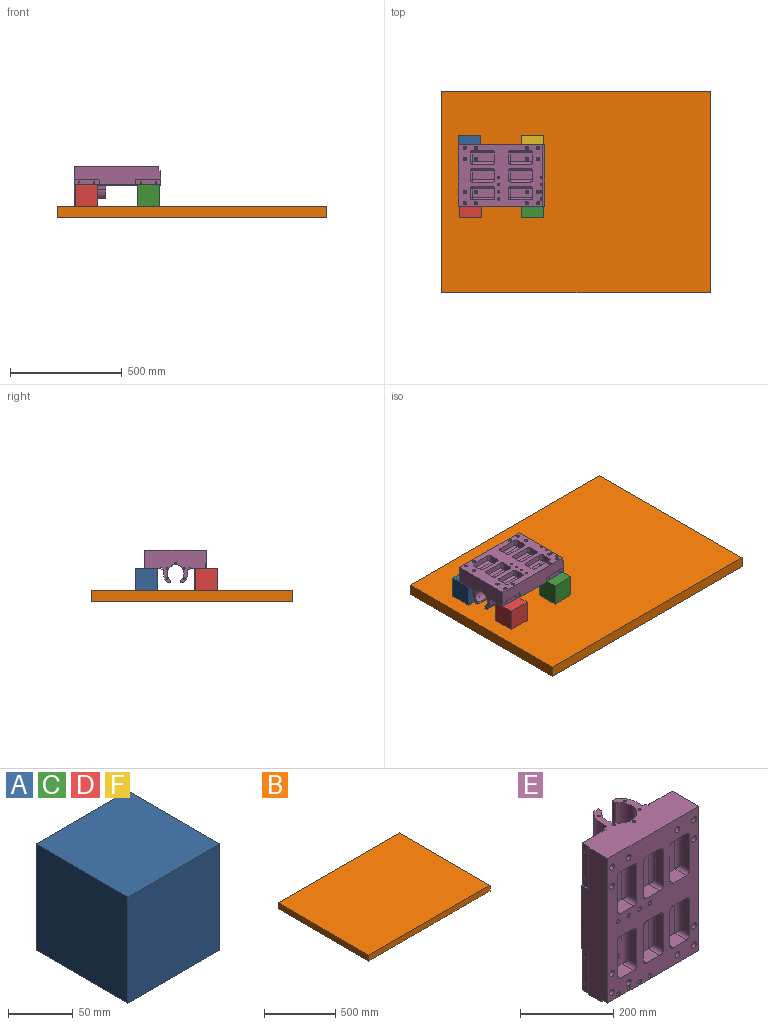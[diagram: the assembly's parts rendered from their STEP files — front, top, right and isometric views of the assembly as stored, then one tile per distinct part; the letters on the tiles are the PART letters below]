
ASSEMBLY  parts=6 mates=5
PART A: 6 faces, bbox 100x100x100 mm
  f0: plane 100x100mm, normal (0,0,1), area 10000mm2, adj f1,f3,f4,f5
  f1: plane 100x100mm, normal (-1,0,0), area 10000mm2, adj f0,f2,f4,f5
  f2: plane 100x100mm, normal (0,0,-1), area 10000mm2, adj f1,f3,f4,f5
  f3: plane 100x100mm, normal (1,0,0), area 10000mm2, adj f0,f2,f4,f5
  f4: plane 100x100mm, normal (0,-1,0), area 10000mm2, adj f0,f1,f2,f3
  f5: plane 100x100mm, normal (0,1,0), area 10000mm2, adj f0,f1,f2,f3
PART B: 6 faces, bbox 1200x900x50 mm
  f0: plane 1200x50mm, normal (0,1,0), area 60000mm2, adj f1,f3,f4,f5
  f1: plane 900x50mm, normal (-1,0,0), area 45000mm2, adj f0,f2,f4,f5
  f2: plane 1200x50mm, normal (0,-1,0), area 60000mm2, adj f1,f3,f4,f5
  f3: plane 900x50mm, normal (1,0,0), area 45000mm2, adj f0,f2,f4,f5
  f4: plane 1200x900mm, normal (0,0,1), area 1080000mm2, adj f0,f1,f2,f3
  f5: plane 1200x900mm, normal (0,0,-1), area 1080000mm2, adj f0,f1,f2,f3
PART C: same geometry as A
PART D: same geometry as A
PART E: 238 faces, bbox 275x144.8x385 mm
  f0: plane 139x14mm, normal (0,1,0), area 1946mm2, adj f2,f7,f10,f214
  f1: plane 378x275mm, normal (0,-1,0), area 62109.9mm2, adj f4,f6,f7,f42,f43,f44,f45,f47
  f2: plane 109.04x90mm, normal (0,0,-1), area 3910.3mm2, adj f0,f3,f8,f9,f10,f11,f12,f13
  f3: plane 139x17mm, normal (-1,0,0), area 2363mm2, adj f2,f7,f8,f24
  f4: plane 385x80mm, normal (-1,0,0), area 25610.7mm2, adj f1,f5,f7,f16,f18,f19,f198,f199
  f5: plane 275x66mm, normal (0,0,-1), area 14398.7mm2, adj f4,f6,f12,f13,f14,f15,f16,f17
  f6: plane 385x80mm, normal (1,0,0), area 30546.9mm2, adj f1,f5,f7,f17,f198,f199,f231,f233
  f7: plane 275x144.8mm, normal (0,0,1), area 23627.4mm2, adj f0,f1,f3,f4,f6,f8,f9,f10
  f8: cylinder r=54.52mm len=139mm, axis (0,0,1), area 6621mm2, adj f2,f3,f7,f9
  f9: plane 139x14mm, normal (0,1,0), area 1946mm2, adj f2,f7,f8,f213
  f10: cylinder r=54.52mm len=139mm, axis (0,0,1), area 6621mm2, adj f0,f2,f7,f11
  f11: plane 139x17mm, normal (1,0,0), area 2363mm2, adj f2,f7,f10,f22
  f12: plane 246x30mm, normal (0.85,0.52,0), area 8650mm2, adj f2,f5,f13,f23
  f13: plane 246x70mm, normal (0,1,0), area 17220mm2, adj f2,f5,f12,f14
  f14: plane 246x30mm, normal (-0.85,0.52,0), area 8650mm2, adj f2,f5,f13,f21
  f15: plane 385x8mm, normal (1,0,0), area 3080mm2, adj f5,f7,f22,f218
  f16: plane 385x69mm, normal (0,1,0), area 25396.1mm2, adj f4,f5,f7,f18,f20,f126,f129,f133
  f17: plane 385x71mm, normal (0,1,0), area 26826.1mm2, adj f5,f6,f7,f138,f141,f144,f147,f156
  f18: plane 18x3mm, normal (0,0,-1), area 54mm2, adj f4,f16,f20,f228
  f19: plane 105x3mm, normal (0,1,0), area 315mm2, adj f4,f5,f20,f228
  f20: plane 110x23mm, normal (-1,0,0), area 2467.1mm2, adj f5,f16,f18,f19,f28,f31,f228
  f21: plane 246x1.2mm, normal (-1,0,0), area 295.2mm2, adj f2,f5,f14,f22
  f22: plane 385x9.16mm, normal (0,1,0), area 3362.5mm2, adj f2,f5,f7,f11,f15,f21
  f23: plane 246x1.2mm, normal (1,0,0), area 295.2mm2, adj f2,f5,f12,f24
  f24: plane 385x11.16mm, normal (0,1,0), area 4132.5mm2, adj f2,f3,f5,f7,f23,f25
  f25: plane 385x8mm, normal (-1,0,0), area 3080mm2, adj f5,f7,f24,f215
  f26: cone r=2.5mm half-angle=59deg, axis (-1,0,0), area 22.9mm2, adj f27
  f27: cylinder r=2.5mm len=14.48mm, axis (-1,0,0), area 227.4mm2, adj f26,f28
  f28: cone r=3.02mm half-angle=45deg, axis (-1,0,0), area 12.9mm2, adj f20,f27
  f29: cone r=2.5mm half-angle=59deg, axis (-1,0,0), area 22.9mm2, adj f30
  f30: cylinder r=2.5mm len=14.48mm, axis (-1,0,0), area 227.4mm2, adj f29,f31
  f31: cone r=3.02mm half-angle=45deg, axis (-1,0,0), area 12.9mm2, adj f20,f30
  f32: cone r=3.4mm half-angle=59deg, axis (0,0,1), area 42.4mm2, adj f33
  f33: cylinder r=3.4mm len=23.8mm, axis (0,0,1), area 508.4mm2, adj f7,f32
  f34: cone r=3.4mm half-angle=59deg, axis (0,0,1), area 42.4mm2, adj f35
  f35: cylinder r=3.4mm len=23.8mm, axis (0,0,1), area 508.4mm2, adj f7,f34
  f36: cone r=3.4mm half-angle=59deg, axis (0,0,1), area 42.4mm2, adj f37
  f37: cylinder r=3.4mm len=23.8mm, axis (0,0,1), area 508.4mm2, adj f7,f36
  f38: cone r=3.4mm half-angle=59deg, axis (0,0,1), area 42.4mm2, adj f39
  f39: cylinder r=3.4mm len=23.8mm, axis (0,0,1), area 508.4mm2, adj f7,f38
  f40: cone r=3.4mm half-angle=59deg, axis (0,0,1), area 42.4mm2, adj f41
  f41: cylinder r=3.4mm len=23.8mm, axis (0,0,1), area 508.4mm2, adj f7,f40
  f42: plane 90x25mm, normal (1,0,0), area 2250mm2, adj f1,f90,f91,f92
  f43: plane 40x25mm, normal (0,0,-1), area 1000mm2, adj f1,f92,f94,f95
  f44: plane 90x25mm, normal (-1,0,0), area 2250mm2, adj f1,f95,f97,f98
  f45: plane 40x35mm, normal (0,0,1), area 1400mm2, adj f1,f46,f90,f98
  f46: plane 100x40mm, normal (0,-1,0), area 3823.3mm2, adj f45,f91,f94,f97,f155
  f47: plane 90x25mm, normal (1,0,0), area 2250mm2, adj f1,f72,f73,f74
  f48: plane 40x25mm, normal (0,0,-1), area 1000mm2, adj f1,f74,f78,f80
  f49: plane 90x25mm, normal (-1,0,0), area 2250mm2, adj f1,f75,f77,f80
  f50: plane 40x35mm, normal (0,0,1), area 1400mm2, adj f1,f51,f72,f75
  f51: plane 100x40mm, normal (0,-1,0), area 4000mm2, adj f50,f73,f77,f78
  f52: plane 90x25mm, normal (1,0,0), area 2250mm2, adj f1,f81,f82,f83
  f53: plane 40x25mm, normal (0,0,-1), area 1000mm2, adj f1,f83,f87,f89
  f54: plane 90x25mm, normal (-1,0,0), area 2250mm2, adj f1,f84,f86,f89
  f55: plane 40x35mm, normal (0,0,1), area 1400mm2, adj f1,f56,f81,f84
  f56: plane 100x40mm, normal (0,-1,0), area 3823.3mm2, adj f55,f82,f86,f87,f158
  f57: plane 40x35mm, normal (0,0,1), area 1400mm2, adj f1,f61,f99,f107
  f58: plane 90x25mm, normal (1,0,0), area 2250mm2, adj f1,f103,f106,f107
  f59: plane 40x25mm, normal (0,0,-1), area 1000mm2, adj f1,f100,f103,f104
  f60: plane 90x25mm, normal (-1,0,0), area 2250mm2, adj f1,f99,f100,f101
  f61: plane 100x40mm, normal (0,-1,0), area 3823.3mm2, adj f57,f101,f104,f106,f149
  f62: plane 90x25mm, normal (1,0,0), area 2250mm2, adj f1,f112,f115,f116
  f63: plane 40x25mm, normal (0,0,-1), area 1000mm2, adj f1,f109,f112,f113
  f64: plane 90x25mm, normal (-1,0,0), area 2250mm2, adj f1,f108,f109,f110
  f65: plane 40x35mm, normal (0,0,1), area 1400mm2, adj f1,f66,f108,f116
  f66: plane 100x40mm, normal (0,-1,0), area 4000mm2, adj f65,f110,f113,f115
  f67: plane 90x25mm, normal (1,0,0), area 2250mm2, adj f1,f121,f124,f125
  f68: plane 40x25mm, normal (0,0,-1), area 1000mm2, adj f1,f118,f121,f122
  f69: plane 90x25mm, normal (-1,0,0), area 2250mm2, adj f1,f117,f118,f119
  f70: plane 40x35mm, normal (0,0,1), area 1400mm2, adj f1,f71,f117,f125
  f71: plane 100x40mm, normal (0,-1,0), area 3823.3mm2, adj f70,f119,f122,f124,f132
  f72: cylinder r=10mm len=35mm, axis (0,1,0), area 492.7mm2, adj f1,f47,f50,f73
  f73: cylinder r=10mm len=100mm, axis (0,0,-1), area 1513.7mm2, adj f47,f51,f72,f76
  f74: cylinder r=10mm len=25mm, axis (0,1,0), area 392.7mm2, adj f1,f47,f48,f76
  f75: cylinder r=10mm len=35mm, axis (0,1,0), area 492.7mm2, adj f1,f49,f50,f77
  f76: sphere r=10mm, area 157.1mm2, adj f73,f74,f78
  f77: cylinder r=10mm len=100mm, axis (0,0,1), area 1513.7mm2, adj f49,f51,f75,f79
  f78: cylinder r=10mm len=40mm, axis (-1,0,0), area 628.3mm2, adj f48,f51,f76,f79
  f79: sphere r=10mm, area 157.1mm2, adj f77,f78,f80
  f80: cylinder r=10mm len=25mm, axis (0,1,0), area 392.7mm2, adj f1,f48,f49,f79
  f81: cylinder r=10mm len=35mm, axis (0,1,0), area 492.7mm2, adj f1,f52,f55,f82
  f82: cylinder r=10mm len=100mm, axis (0,0,-1), area 1513.7mm2, adj f52,f56,f81,f85
  f83: cylinder r=10mm len=25mm, axis (0,1,0), area 392.7mm2, adj f1,f52,f53,f85
  f84: cylinder r=10mm len=35mm, axis (0,1,0), area 492.7mm2, adj f1,f54,f55,f86
  f85: sphere r=10mm, area 157.1mm2, adj f82,f83,f87
  f86: cylinder r=10mm len=100mm, axis (0,0,1), area 1513.7mm2, adj f54,f56,f84,f88
  f87: cylinder r=10mm len=40mm, axis (-1,0,0), area 628.3mm2, adj f53,f56,f85,f88
  f88: sphere r=10mm, area 157.1mm2, adj f86,f87,f89
  f89: cylinder r=10mm len=25mm, axis (0,1,0), area 392.7mm2, adj f1,f53,f54,f88
  f90: cylinder r=10mm len=35mm, axis (0,1,0), area 492.7mm2, adj f1,f42,f45,f91
  f91: cylinder r=10mm len=100mm, axis (0,0,-1), area 1513.7mm2, adj f42,f46,f90,f93
  f92: cylinder r=10mm len=25mm, axis (0,1,0), area 392.7mm2, adj f1,f42,f43,f93
  f93: sphere r=10mm, area 157.1mm2, adj f91,f92,f94
  f94: cylinder r=10mm len=40mm, axis (-1,0,0), area 628.3mm2, adj f43,f46,f93,f96
  f95: cylinder r=10mm len=25mm, axis (0,1,0), area 392.7mm2, adj f1,f43,f44,f96
  f96: sphere r=10mm, area 157.1mm2, adj f94,f95,f97
  f97: cylinder r=10mm len=100mm, axis (0,0,1), area 1513.7mm2, adj f44,f46,f96,f98
  f98: cylinder r=10mm len=35mm, axis (0,1,0), area 492.7mm2, adj f1,f44,f45,f97
  f99: cylinder r=10mm len=35mm, axis (0,1,0), area 492.7mm2, adj f1,f57,f60,f101
  f100: cylinder r=10mm len=25mm, axis (0,1,0), area 392.7mm2, adj f1,f59,f60,f102
  f101: cylinder r=10mm len=100mm, axis (0,0,1), area 1513.7mm2, adj f60,f61,f99,f102
  f102: sphere r=10mm, area 157.1mm2, adj f100,f101,f104
  f103: cylinder r=10mm len=25mm, axis (0,1,0), area 392.7mm2, adj f1,f58,f59,f105
  f104: cylinder r=10mm len=40mm, axis (-1,0,0), area 628.3mm2, adj f59,f61,f102,f105
  f105: sphere r=10mm, area 157.1mm2, adj f103,f104,f106
  f106: cylinder r=10mm len=100mm, axis (0,0,-1), area 1513.7mm2, adj f58,f61,f105,f107
  f107: cylinder r=10mm len=35mm, axis (0,1,0), area 492.7mm2, adj f1,f57,f58,f106
  f108: cylinder r=10mm len=35mm, axis (0,1,0), area 492.7mm2, adj f1,f64,f65,f110
  f109: cylinder r=10mm len=25mm, axis (0,1,0), area 392.7mm2, adj f1,f63,f64,f111
  f110: cylinder r=10mm len=100mm, axis (0,0,-1), area 1513.7mm2, adj f64,f66,f108,f111
  f111: sphere r=10mm, area 157.1mm2, adj f109,f110,f113
  f112: cylinder r=10mm len=25mm, axis (0,1,0), area 392.7mm2, adj f1,f62,f63,f114
  f113: cylinder r=10mm len=40mm, axis (1,0,0), area 628.3mm2, adj f63,f66,f111,f114
  f114: sphere r=10mm, area 157.1mm2, adj f112,f113,f115
  f115: cylinder r=10mm len=100mm, axis (0,0,1), area 1513.7mm2, adj f62,f66,f114,f116
  f116: cylinder r=10mm len=35mm, axis (0,1,0), area 492.7mm2, adj f1,f62,f65,f115
  f117: cylinder r=10mm len=35mm, axis (0,1,0), area 492.7mm2, adj f1,f69,f70,f119
  f118: cylinder r=10mm len=25mm, axis (0,1,0), area 392.7mm2, adj f1,f68,f69,f120
  f119: cylinder r=10mm len=100mm, axis (0,0,-1), area 1513.7mm2, adj f69,f71,f117,f120
  f120: sphere r=10mm, area 157.1mm2, adj f118,f119,f122
  f121: cylinder r=10mm len=25mm, axis (0,1,0), area 392.7mm2, adj f1,f67,f68,f123
  f122: cylinder r=10mm len=40mm, axis (1,0,0), area 628.3mm2, adj f68,f71,f120,f123
  f123: sphere r=10mm, area 157.1mm2, adj f121,f122,f124
  f124: cylinder r=10mm len=100mm, axis (0,0,1), area 1513.7mm2, adj f67,f71,f123,f125
  f125: cylinder r=10mm len=35mm, axis (0,1,0), area 492.7mm2, adj f1,f67,f70,f124
  f126: cylinder r=4.5mm len=30mm, axis (0,-1,0), area 848.2mm2, adj f16,f127
  f127: plane 15x15mm, normal (0,-1,0), area 113.1mm2, adj f126,f128
  f128: cylinder r=7.5mm len=50mm, axis (0,-1,0), area 2356.2mm2, adj f1,f127
  f129: cylinder r=4.5mm len=30mm, axis (0,-1,0), area 848.2mm2, adj f16,f130
  f130: plane 15x15mm, normal (0,-1,0), area 113.1mm2, adj f129,f131
  f131: cylinder r=7.5mm len=50mm, axis (0,-1,0), area 2356.2mm2, adj f1,f130
  f132: cylinder r=7.5mm len=15mm, axis (0,-1,0), area 706.9mm2, adj f71,f134
  f133: cylinder r=4.5mm len=30mm, axis (0,-1,0), area 848.2mm2, adj f16,f134
  f134: plane 15x15mm, normal (0,-1,0), area 113.1mm2, adj f132,f133
  f135: cylinder r=4.5mm len=30mm, axis (0,-1,0), area 848.2mm2, adj f16,f136
  f136: plane 15x15mm, normal (0,-1,0), area 113.1mm2, adj f135,f137
  f137: cylinder r=7.5mm len=50mm, axis (0,-1,0), area 2356.2mm2, adj f1,f136
  f138: cylinder r=4.5mm len=30mm, axis (0,-1,0), area 848.2mm2, adj f17,f139
  f139: plane 15x15mm, normal (0,-1,0), area 113.1mm2, adj f138,f140
  f140: cylinder r=7.5mm len=50mm, axis (0,-1,0), area 2356.2mm2, adj f1,f139
  f141: cylinder r=4.5mm len=30mm, axis (0,-1,0), area 848.2mm2, adj f17,f142
  f142: plane 15x15mm, normal (0,-1,0), area 113.1mm2, adj f141,f143
  f143: cylinder r=7.5mm len=50mm, axis (0,-1,0), area 2356.2mm2, adj f1,f142
  f144: cylinder r=4.5mm len=30mm, axis (0,-1,0), area 848.2mm2, adj f17,f145
  f145: plane 15x15mm, normal (0,-1,0), area 113.1mm2, adj f144,f146
  f146: cylinder r=7.5mm len=50mm, axis (0,-1,0), area 2356.2mm2, adj f1,f145
  f147: cylinder r=4.5mm len=30mm, axis (0,-1,0), area 848.2mm2, adj f17,f148
  f148: plane 15x15mm, normal (0,-1,0), area 113.1mm2, adj f147,f149
  f149: cylinder r=7.5mm len=15mm, axis (0,-1,0), area 706.9mm2, adj f61,f148
  f150: cylinder r=4.5mm len=30mm, axis (0,-1,0), area 848.2mm2, adj f16,f151
  f151: plane 15x15mm, normal (0,-1,0), area 113.1mm2, adj f150,f152
  f152: cylinder r=7.5mm len=50mm, axis (0,-1,0), area 2356.2mm2, adj f1,f151
  f153: cylinder r=4.5mm len=30mm, axis (0,-1,0), area 848.2mm2, adj f16,f154
  f154: plane 15x15mm, normal (0,-1,0), area 113.1mm2, adj f153,f155
  f155: cylinder r=7.5mm len=15mm, axis (0,-1,0), area 706.9mm2, adj f46,f154
  f156: cylinder r=4.5mm len=30mm, axis (0,-1,0), area 848.2mm2, adj f17,f157
  f157: plane 15x15mm, normal (0,-1,0), area 113.1mm2, adj f156,f158
  f158: cylinder r=7.5mm len=15mm, axis (0,-1,0), area 706.9mm2, adj f56,f157
  f159: cylinder r=4.5mm len=30mm, axis (0,-1,0), area 848.2mm2, adj f17,f160
  f160: plane 15x15mm, normal (0,-1,0), area 113.1mm2, adj f159,f161
  f161: cylinder r=7.5mm len=50mm, axis (0,-1,0), area 2356.2mm2, adj f1,f160
  f162: cylinder r=4.5mm len=30mm, axis (0,-1,0), area 848.2mm2, adj f17,f163
  f163: plane 15x15mm, normal (0,-1,0), area 113.1mm2, adj f162,f164
  f164: cylinder r=7.5mm len=50mm, axis (0,-1,0), area 2356.2mm2, adj f1,f163
  f165: cylinder r=4.5mm len=30mm, axis (0,-1,0), area 848.2mm2, adj f17,f166
  f166: plane 15x15mm, normal (0,-1,0), area 113.1mm2, adj f165,f167
  f167: cylinder r=7.5mm len=50mm, axis (0,-1,0), area 2356.2mm2, adj f1,f166
  f168: cylinder r=4.5mm len=30mm, axis (0,-1,0), area 848.2mm2, adj f16,f169
  f169: plane 15x15mm, normal (0,-1,0), area 113.1mm2, adj f168,f170
  f170: cylinder r=7.5mm len=50mm, axis (0,-1,0), area 2356.2mm2, adj f1,f169
  f171: cylinder r=4.5mm len=30mm, axis (0,-1,0), area 848.2mm2, adj f16,f172
  f172: plane 15x15mm, normal (0,-1,0), area 113.1mm2, adj f171,f173
  f173: cylinder r=7.5mm len=50mm, axis (0,-1,0), area 2356.2mm2, adj f1,f172
  f174: cone r=4.4mm half-angle=59deg, axis (0,-1,0), area 71mm2, adj f175
  f175: cylinder r=4.4mm len=23.18mm, axis (0,-1,0), area 640.7mm2, adj f174,f176
  f176: cone r=5.03mm half-angle=45deg, axis (0,-1,0), area 26.2mm2, adj f1,f175
  f177: cone r=4.4mm half-angle=59deg, axis (0,-1,0), area 71mm2, adj f178
  f178: cylinder r=4.4mm len=23.18mm, axis (0,-1,0), area 640.7mm2, adj f177,f179
  f179: cone r=5.03mm half-angle=45deg, axis (0,-1,0), area 26.2mm2, adj f1,f178
  f180: cone r=4.4mm half-angle=59deg, axis (0,-1,0), area 71mm2, adj f181
  f181: cylinder r=4.4mm len=23.18mm, axis (0,-1,0), area 640.7mm2, adj f180,f182
  f182: cone r=5.03mm half-angle=45deg, axis (0,-1,0), area 26.2mm2, adj f1,f181
  f183: cone r=4.4mm half-angle=59deg, axis (0,-1,0), area 71mm2, adj f184
  f184: cylinder r=4.4mm len=23.18mm, axis (0,-1,0), area 640.7mm2, adj f183,f185
  f185: cone r=5.03mm half-angle=45deg, axis (0,-1,0), area 26.2mm2, adj f1,f184
  f186: cone r=4.4mm half-angle=59deg, axis (0,-1,0), area 71mm2, adj f187
  f187: cylinder r=4.4mm len=23.18mm, axis (0,-1,0), area 640.7mm2, adj f186,f188
  f188: cone r=5.03mm half-angle=45deg, axis (0,-1,0), area 26.2mm2, adj f1,f187
  f189: cone r=4.4mm half-angle=59deg, axis (0,-1,0), area 71mm2, adj f190
  f190: cylinder r=4.4mm len=23.18mm, axis (0,-1,0), area 640.7mm2, adj f189,f191
  f191: cone r=5.03mm half-angle=45deg, axis (0,-1,0), area 26.2mm2, adj f1,f190
  f192: cone r=4.4mm half-angle=59deg, axis (0,-1,0), area 71mm2, adj f193
  f193: cylinder r=4.4mm len=23.18mm, axis (0,-1,0), area 640.7mm2, adj f192,f194
  f194: cone r=5.03mm half-angle=45deg, axis (0,-1,0), area 26.2mm2, adj f1,f193
  f195: cone r=4.4mm half-angle=59deg, axis (0,-1,0), area 71mm2, adj f196
  f196: cylinder r=4.4mm len=23.18mm, axis (0,-1,0), area 640.7mm2, adj f195,f197
  f197: cone r=5.03mm half-angle=45deg, axis (0,-1,0), area 26.2mm2, adj f1,f196
  f198: plane 275x7mm, normal (0,-1,0), area 1925mm2, adj f4,f5,f6,f199
  f199: plane 275x20mm, normal (0,0,-1), area 5296.4mm2, adj f1,f4,f6,f198,f202,f205,f208,f211
  f200: cone r=3.4mm half-angle=59deg, axis (0,0,-1), area 42.4mm2, adj f201
  f201: cylinder r=3.4mm len=19.18mm, axis (0,0,-1), area 409.6mm2, adj f200,f202
  f202: cone r=4.03mm half-angle=45deg, axis (0,0,-1), area 20.6mm2, adj f199,f201
  f203: cone r=3.4mm half-angle=59deg, axis (0,0,-1), area 42.4mm2, adj f204
  f204: cylinder r=3.4mm len=19.18mm, axis (0,0,-1), area 409.6mm2, adj f203,f205
  f205: cone r=4.03mm half-angle=45deg, axis (0,0,-1), area 20.6mm2, adj f199,f204
  f206: cone r=3.4mm half-angle=59deg, axis (0,0,-1), area 42.4mm2, adj f207
  f207: cylinder r=3.4mm len=19.18mm, axis (0,0,-1), area 409.6mm2, adj f206,f208
  f208: cone r=4.03mm half-angle=45deg, axis (0,0,-1), area 20.6mm2, adj f199,f207
  f209: cone r=3.4mm half-angle=59deg, axis (0,0,-1), area 42.4mm2, adj f210
  f210: cylinder r=3.4mm len=19.18mm, axis (0,0,-1), area 409.6mm2, adj f209,f211
  f211: cone r=4.03mm half-angle=45deg, axis (0,0,-1), area 20.6mm2, adj f199,f210
  f212: cylinder r=38mm len=139mm, axis (0,0,1), area 27002.4mm2, adj f2,f7,f213,f214
  f213: plane 139x10.13mm, normal (1,0,0), area 1408mm2, adj f2,f7,f9,f212
  f214: plane 139x10.13mm, normal (-1,0,0), area 1408mm2, adj f0,f2,f7,f212
  f215: plane 385x4mm, normal (0,1,0), area 1540mm2, adj f5,f7,f25,f216
  f216: plane 385x2mm, normal (1,0,0), area 770mm2, adj f5,f7,f16,f215
  f217: plane 385x2mm, normal (-1,0,0), area 770mm2, adj f5,f7,f17,f218
  f218: plane 385x4mm, normal (0,1,0), area 1540mm2, adj f5,f7,f15,f217
  f219: plane 105x3mm, normal (0,1,0), area 315mm2, adj f4,f7,f221,f229
  f220: plane 18x3mm, normal (0,0,1), area 54mm2, adj f4,f16,f221,f229
  f221: plane 110x23mm, normal (-1,0,0), area 2467.1mm2, adj f7,f16,f219,f220,f224,f227,f229
  f222: cone r=2.5mm half-angle=59deg, axis (-1,0,0), area 22.9mm2, adj f223
  f223: cylinder r=2.5mm len=14.48mm, axis (-1,0,0), area 227.4mm2, adj f222,f224
  f224: cone r=3.02mm half-angle=45deg, axis (-1,0,0), area 12.9mm2, adj f221,f223
  f225: cone r=2.5mm half-angle=59deg, axis (-1,0,0), area 22.9mm2, adj f226
  f226: cylinder r=2.5mm len=14.48mm, axis (-1,0,0), area 227.4mm2, adj f225,f227
  f227: cone r=3.02mm half-angle=45deg, axis (-1,0,0), area 12.9mm2, adj f221,f226
  f228: cylinder r=5mm len=5mm, axis (1,0,0), area 23.6mm2, adj f4,f18,f19,f20
  f229: cylinder r=5mm len=5mm, axis (1,0,0), area 23.6mm2, adj f4,f219,f220,f221
  f230: cone r=3mm half-angle=59deg, axis (1,0,0), area 33mm2, adj f231
  f231: cylinder r=3mm len=20mm, axis (1,0,0), area 377mm2, adj f6,f230
  f232: cone r=3mm half-angle=59deg, axis (1,0,0), area 33mm2, adj f233
  f233: cylinder r=3mm len=20mm, axis (1,0,0), area 377mm2, adj f6,f232
  f234: cone r=3mm half-angle=59deg, axis (1,0,0), area 33mm2, adj f235
  f235: cylinder r=3mm len=20mm, axis (1,0,0), area 377mm2, adj f6,f234
  f236: cone r=3mm half-angle=59deg, axis (1,0,0), area 33mm2, adj f237
  f237: cylinder r=3mm len=20mm, axis (1,0,0), area 377mm2, adj f6,f236
PART F: same geometry as A
PLACE A t=(-607.51,-132.78,-473.6)mm
PLACE B t=(-458.46,-700.2,-532.79)mm
PLACE C rot(axis=(0,0.71,0.71),180deg) t=(-251.4,-490,-382.79)mm
PLACE D rot(axis=(1,0,0),90deg) t=(-605.18,-409.18,-382.79)mm
PLACE E rot(axis=(-0.58,-0.58,0.58),120deg) t=(-620.03,-341.42,-334.29)mm
PLACE F rot(axis=(1,0,0),180deg) t=(-325.83,-232.08,-391.98)mm
MATE planar E.f16 <-> D.f5  axis (0,0,-1) through (-427.53,-414.74,-382.79)mm
MATE planar F.f0 <-> B.f4  axis (0,0,-1) through (-287.92,-182.08,-482.79)mm
MATE planar C.f4 <-> B.f4  axis (0,0,-1) through (-289.31,-449.19,-482.79)mm
MATE planar D.f4 <-> B.f4  axis (0,0,-1) through (-567.27,-450,-482.79)mm
MATE planar A.f2 <-> B.f4  axis (0,0,-1) through (-569.59,-182.78,-482.79)mm
